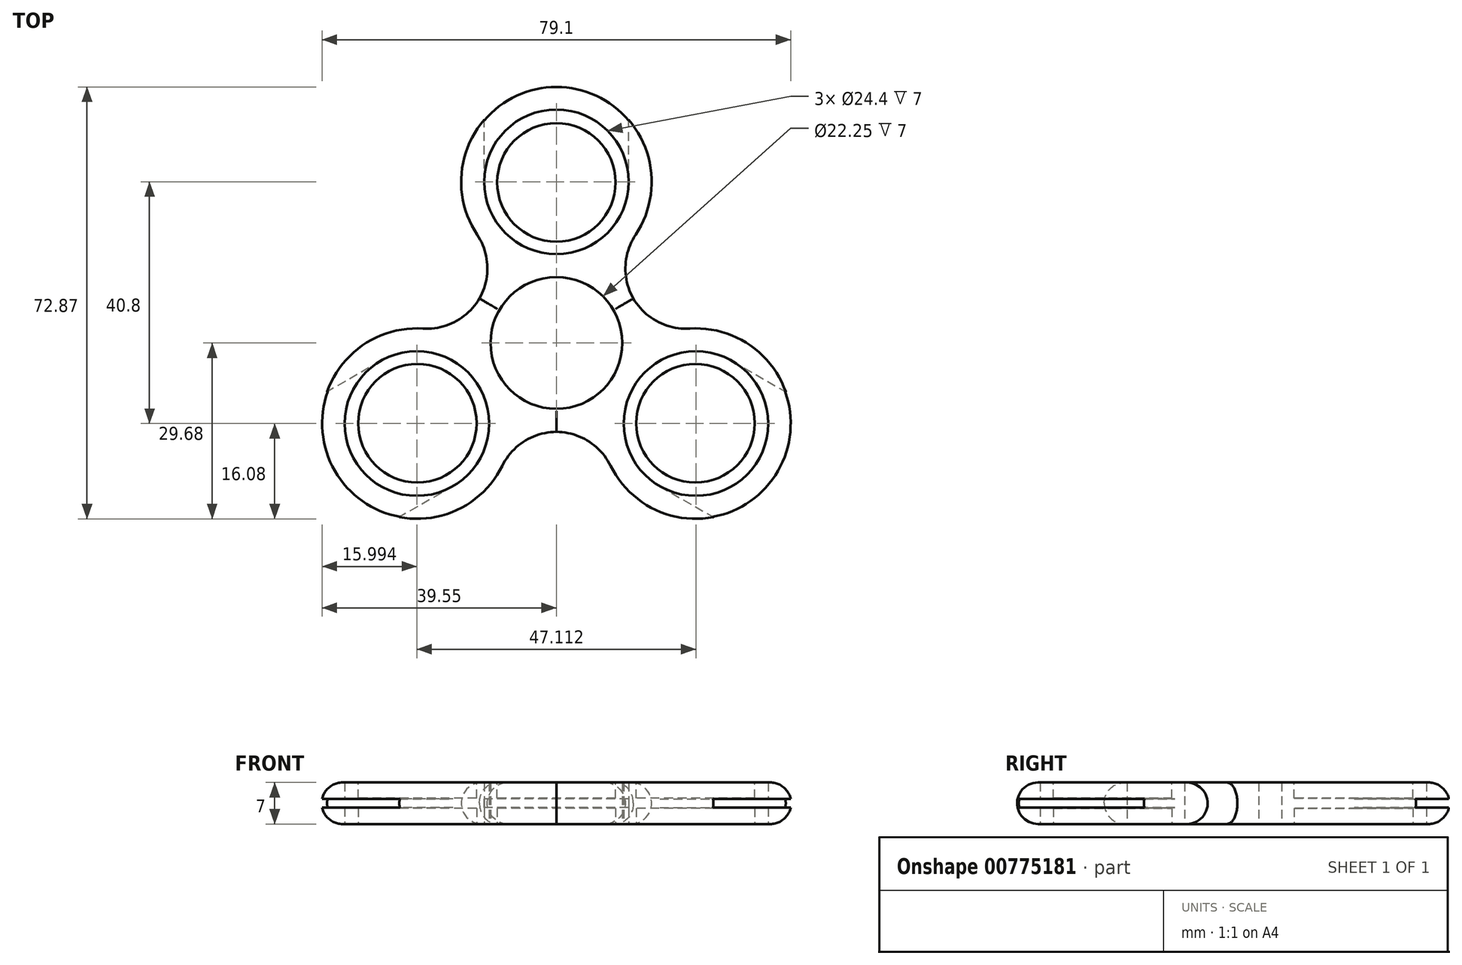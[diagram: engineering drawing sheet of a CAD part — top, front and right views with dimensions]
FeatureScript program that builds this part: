
annotation { "Feature Type Name" : "Feature", "Feature Type Description" : "" }
export const myFeature = defineFeature(function(context is Context, id is Id, definition is map)
    precondition{}
    {
        {
            var Q0;
            Q0=qCreatedBy(makeId("Top.planeOp"),FACE);
            var sketch = newSketch(context, id + "F0", { "sketchPlane" : qUnion([Q0])});
            skCircle(sketch, "E0", {"center": v(0, 0) * mm, "radius": 15 * mm});
            skCircle(sketch, "E1", {"center": v(0, 0) * mm, "radius": 11.12 * mm});
            skCircle(sketch, "E2", {"center": v(0, 27.2) * mm, "radius": 12.2 * mm});
            skCircle(sketch, "E3", {"center": v(0, 27.2) * mm, "radius": 16.07 * mm});
            skLineSegment(sketch, "E4", {"start": v(-12.2, 27.2) * mm, "end": v(-12.2, 47.2) * mm});
            skLineSegment(sketch, "E5.MirrorCS", {"start": v(12.2, 27.2) * mm, "end": v(12.2, 47.2) * mm});
            skLineSegment(sketch, "E6", {"start": v(-12.2, 47.2) * mm, "end": v(12.2, 47.2) * mm});
            skCircle(sketch, "E7.MirrorC", {"center": v(0, 27.1) * mm, "radius": 10 * mm});
            skCircle(sketch, "E8.1.0", {"center": v(-23.56, -13.6) * mm, "radius": 16.07 * mm});
            skCircle(sketch, "E8.1.1", {"center": v(-23.56, -13.6) * mm, "radius": 12.2 * mm});
            skCircle(sketch, "E8.1.2", {"center": v(-23.47, -13.55) * mm, "radius": 10 * mm});
            skLineSegment(sketch, "E8.1.3", {"start": v(-17.46, -24.17) * mm, "end": v(-34.78, -34.17) * mm});
            skLineSegment(sketch, "E8.1.4", {"start": v(-34.78, -34.17) * mm, "end": v(-46.98, -13.03) * mm});
            skLineSegment(sketch, "E8.1.5", {"start": v(-29.66, -3.03) * mm, "end": v(-46.98, -13.03) * mm});
            skCircle(sketch, "E8.2.0", {"center": v(23.56, -13.6) * mm, "radius": 16.07 * mm});
            skCircle(sketch, "E8.2.1", {"center": v(23.56, -13.6) * mm, "radius": 12.2 * mm});
            skCircle(sketch, "E8.2.2", {"center": v(23.47, -13.55) * mm, "radius": 10 * mm});
            skLineSegment(sketch, "E8.2.3", {"start": v(29.66, -3.03) * mm, "end": v(46.98, -13.03) * mm});
            skLineSegment(sketch, "E8.2.4", {"start": v(46.98, -13.03) * mm, "end": v(34.78, -34.17) * mm});
            skLineSegment(sketch, "E8.2.5", {"start": v(17.46, -24.17) * mm, "end": v(34.78, -34.17) * mm});
            skSolve(sketch);
        }
        {
            var Q0;
            {var subQ0=sQuery(id+"F0.wireOp",EDGE,"E3");var subQ1=sQuery(id+"F0.wireOp",EDGE,"E0");var subQ2=makeQuery(id+"F0.imprint","INTERSECT",VERTEX,{"disambiguationData":[OD(0.0)],"derivedFrom":[subQ1,subQ0]});Q0=makeQuery(id+"F0.imprint","IMPRINT",FACE,{"disambiguationData":[TD([[makeQuery(id+"F0.imprint","IMPRINT",EDGE,{"disambiguationData":[TD([[subQ2,-1.0]])],"derivedFrom":subQ1}),-1.0]])]});}
            var Q1;
            {var subQ0=sQuery(id+"F0.wireOp",EDGE,"E3");var subQ1=sQuery(id+"F0.wireOp",EDGE,"E0");var subQ2=makeQuery(id+"F0.imprint","INTERSECT",VERTEX,{"disambiguationData":[OD(1.0)],"derivedFrom":[subQ1,subQ0]});Q1=makeQuery(id+"F0.imprint","IMPRINT",FACE,{"disambiguationData":[TD([[makeQuery(id+"F0.imprint","IMPRINT",EDGE,{"disambiguationData":[TD([[subQ2,1.0]])],"derivedFrom":subQ1}),-1.0]])]});}
            var Q2;
            {var subQ0=sQuery(id+"F0.wireOp",EDGE,"E3");var subQ1=sQuery(id+"F0.wireOp",EDGE,"E0");var subQ2=makeQuery(id+"F0.imprint","INTERSECT",VERTEX,{"disambiguationData":[OD(1.0)],"derivedFrom":[subQ1,subQ0]});Q2=makeQuery(id+"F0.imprint","IMPRINT",FACE,{"disambiguationData":[TD([[makeQuery(id+"F0.imprint","IMPRINT",EDGE,{"disambiguationData":[TD([[subQ2,-1.0]])],"derivedFrom":subQ1}),1.0]])]});}
            var Q3;
            {var subQ0=sQuery(id+"F0.wireOp",EDGE,"E3");var subQ1=sQuery(id+"F0.wireOp",EDGE,"E0");var subQ2=makeQuery(id+"F0.imprint","INTERSECT",VERTEX,{"disambiguationData":[OD(0.0)],"derivedFrom":[subQ1,subQ0]});Q3=makeQuery(id+"F0.imprint","IMPRINT",FACE,{"disambiguationData":[TD([[makeQuery(id+"F0.imprint","IMPRINT",EDGE,{"disambiguationData":[TD([[subQ2,-1.0]])],"derivedFrom":subQ1}),1.0]])]});}
            var Q4;
            {var subQ0=sQuery(id+"F0.wireOp",EDGE,"E3");var subQ1=sQuery(id+"F0.wireOp",EDGE,"E0");var subQ2=makeQuery(id+"F0.imprint","INTERSECT",VERTEX,{"disambiguationData":[OD(0.0)],"derivedFrom":[subQ1,subQ0]});Q4=makeQuery(id+"F0.imprint","IMPRINT",FACE,{"disambiguationData":[TD([[makeQuery(id+"F0.imprint","IMPRINT",EDGE,{"disambiguationData":[TD([[subQ2,1.0]])],"derivedFrom":subQ1}),1.0]])]});}
            var Q5;
            {var subQ0=sQuery(id+"F0.wireOp",EDGE,"f69440ca-244b-4b86-9447-29ce6fa7a21b0.MirrorC");var subQ1=sQuery(id+"F0.wireOp",EDGE,"E0");var subQ2=makeQuery(id+"F0.imprint","INTERSECT",VERTEX,{"disambiguationData":[OD(0.0)],"derivedFrom":[subQ1,subQ0]});Q5=makeQuery(id+"F0.imprint","IMPRINT",FACE,{"disambiguationData":[TD([[makeQuery(id+"F0.imprint","IMPRINT",EDGE,{"disambiguationData":[TD([[subQ2,-1.0]])],"derivedFrom":subQ1}),1.0]])]});}
            var Q6;
            {var subQ0=sQuery(id+"F0.wireOp",EDGE,"f69440ca-244b-4b86-9447-29ce6fa7a21b0.MirrorC");var subQ1=sQuery(id+"F0.wireOp",EDGE,"E0");var subQ2=makeQuery(id+"F0.imprint","INTERSECT",VERTEX,{"disambiguationData":[OD(0.0)],"derivedFrom":[subQ1,subQ0]});Q6=makeQuery(id+"F0.imprint","IMPRINT",FACE,{"disambiguationData":[TD([[makeQuery(id+"F0.imprint","IMPRINT",EDGE,{"disambiguationData":[TD([[subQ2,-1.0]])],"derivedFrom":subQ1}),-1.0]])]});}
            var Q7;
            {var subQ0=sQuery(id+"F0.wireOp",EDGE,"f69440ca-244b-4b86-9447-29ce6fa7a21b0.MirrorC");var subQ1=sQuery(id+"F0.wireOp",EDGE,"E0");var subQ2=makeQuery(id+"F0.imprint","INTERSECT",VERTEX,{"disambiguationData":[OD(1.0)],"derivedFrom":[subQ1,subQ0]});Q7=makeQuery(id+"F0.imprint","IMPRINT",FACE,{"disambiguationData":[TD([[makeQuery(id+"F0.imprint","IMPRINT",EDGE,{"disambiguationData":[TD([[subQ2,1.0]])],"derivedFrom":subQ1}),-1.0]])]});}
            var Q8;
            {var subQ0=sQuery(id+"F0.wireOp",EDGE,"E8.1.0");var subQ1=sQuery(id+"F0.wireOp",EDGE,"E0");var subQ2=makeQuery(id+"F0.imprint","INTERSECT",VERTEX,{"disambiguationData":[OD(0.0)],"derivedFrom":[subQ1,subQ0]});Q8=makeQuery(id+"F0.imprint","IMPRINT",FACE,{"disambiguationData":[TD([[makeQuery(id+"F0.imprint","IMPRINT",EDGE,{"disambiguationData":[TD([[subQ2,-1.0]])],"derivedFrom":subQ1}),-1.0]])]});}
            var Q9;
            {var subQ0=sQuery(id+"F0.wireOp",EDGE,"E8.1.0");var subQ1=sQuery(id+"F0.wireOp",EDGE,"E0");var subQ2=makeQuery(id+"F0.imprint","INTERSECT",VERTEX,{"disambiguationData":[OD(0.0)],"derivedFrom":[subQ1,subQ0]});Q9=makeQuery(id+"F0.imprint","IMPRINT",FACE,{"disambiguationData":[TD([[makeQuery(id+"F0.imprint","IMPRINT",EDGE,{"disambiguationData":[TD([[subQ2,-1.0]])],"derivedFrom":subQ1}),1.0]])]});}
            var Q10;
            {var subQ0=sQuery(id+"F0.wireOp",EDGE,"E8.1.0");var subQ1=sQuery(id+"F0.wireOp",EDGE,"E0");var subQ2=makeQuery(id+"F0.imprint","INTERSECT",VERTEX,{"disambiguationData":[OD(1.0)],"derivedFrom":[subQ1,subQ0]});Q10=makeQuery(id+"F0.imprint","IMPRINT",FACE,{"disambiguationData":[TD([[makeQuery(id+"F0.imprint","IMPRINT",EDGE,{"disambiguationData":[TD([[subQ2,1.0]])],"derivedFrom":subQ1}),-1.0]])]});}
            var Q11;
            {var subQ0=sQuery(id+"F0.wireOp",EDGE,"E8.1.0");var subQ1=sQuery(id+"F0.wireOp",EDGE,"E0");var subQ2=makeQuery(id+"F0.imprint","INTERSECT",VERTEX,{"disambiguationData":[OD(1.0)],"derivedFrom":[subQ1,subQ0]});Q11=makeQuery(id+"F0.imprint","IMPRINT",FACE,{"disambiguationData":[TD([[makeQuery(id+"F0.imprint","IMPRINT",EDGE,{"disambiguationData":[TD([[subQ2,-1.0]])],"derivedFrom":subQ1}),1.0]])]});}
            var Q12;
            {var subQ0=sQuery(id+"F0.wireOp",EDGE,"E8.2.0");var subQ1=sQuery(id+"F0.wireOp",EDGE,"E0");var subQ2=makeQuery(id+"F0.imprint","INTERSECT",VERTEX,{"disambiguationData":[OD(1.0)],"derivedFrom":[subQ1,subQ0]});Q12=makeQuery(id+"F0.imprint","IMPRINT",FACE,{"disambiguationData":[TD([[makeQuery(id+"F0.imprint","IMPRINT",EDGE,{"disambiguationData":[TD([[subQ2,-1.0]])],"derivedFrom":subQ1}),1.0]])]});}
            var Q13;
            {var subQ0=sQuery(id+"F0.wireOp",EDGE,"E8.2.0");var subQ1=sQuery(id+"F0.wireOp",EDGE,"E0");var subQ2=makeQuery(id+"F0.imprint","INTERSECT",VERTEX,{"disambiguationData":[OD(1.0)],"derivedFrom":[subQ1,subQ0]});Q13=makeQuery(id+"F0.imprint","IMPRINT",FACE,{"disambiguationData":[TD([[makeQuery(id+"F0.imprint","IMPRINT",EDGE,{"disambiguationData":[TD([[subQ2,-1.0]])],"derivedFrom":subQ1}),-1.0]])]});}
            var Q14;
            {var subQ0=sQuery(id+"F0.wireOp",EDGE,"E8.2.0");var subQ1=sQuery(id+"F0.wireOp",EDGE,"E0");var subQ2=makeQuery(id+"F0.imprint","INTERSECT",VERTEX,{"disambiguationData":[OD(0.0)],"derivedFrom":[subQ1,subQ0]});Q14=makeQuery(id+"F0.imprint","IMPRINT",FACE,{"disambiguationData":[TD([[makeQuery(id+"F0.imprint","IMPRINT",EDGE,{"disambiguationData":[TD([[subQ2,1.0]])],"derivedFrom":subQ1}),-1.0]])]});}
            extrude(context, id + "F1", {"entities" : qUnion([Q0, Q1, Q2, Q3, Q4, Q5, Q6, Q7, Q8, Q9, Q10, Q11, Q12, Q13, Q14]), "depth" : 7 * mm, "offsetDistance" : 25 * mm});
        }
        {
            var Q0;
            {var subQ0=sQuery(id+"F0.wireOp",EDGE,"v1YN2P9r-Erew-ceTy-kHM2-pDfLZ22rBO5I");var subQ1=sQuery(id+"F0.wireOp",EDGE,"aa156850-8edd-4638-87e1-16b269d65bfe0.MirrorC");var subQ2=makeQuery(id+"F0.imprint","INTERSECT",VERTEX,{"derivedFrom":[subQ1,subQ0]});Q0=makeQuery(id+"F0.imprint","IMPRINT",FACE,{"disambiguationData":[TD([[makeQuery(id+"F0.imprint","IMPRINT",EDGE,{"disambiguationData":[TD([[subQ2,1.0]])],"derivedFrom":subQ1}),1.0]])]});}
            var Q1;
            {var subQ0=sQuery(id+"F0.wireOp",EDGE,"E4");var subQ1=sQuery(id+"F0.wireOp",EDGE,"E2");var subQ2=makeQuery(id+"F0.imprint","INTERSECT",VERTEX,{"derivedFrom":[subQ1,subQ0]});Q1=makeQuery(id+"F0.imprint","IMPRINT",FACE,{"disambiguationData":[TD([[makeQuery(id+"F0.imprint","IMPRINT",EDGE,{"disambiguationData":[TD([[subQ2,1.0]])],"derivedFrom":subQ1}),-1.0]])]});}
            var Q2;
            {var subQ3=sQuery(id+"F0.wireOp",EDGE,"E8.1.0");var subQ5=sQuery(id+"F0.wireOp",EDGE,"E8.1.4");var subQ6=makeQuery(id+"F0.imprint","INTERSECT",VERTEX,{"disambiguationData":[OD(0.0)],"derivedFrom":[subQ3,subQ5]});Q2=makeQuery(id+"F0.imprint","IMPRINT",FACE,{"disambiguationData":[TD([[makeQuery(id+"F0.imprint","IMPRINT",EDGE,{"disambiguationData":[TD([[subQ6,1.0]])],"derivedFrom":subQ3}),1.0]])]});}
            var Q3;
            {var subQ3=sQuery(id+"F0.wireOp",EDGE,"E8.2.0");var subQ5=sQuery(id+"F0.wireOp",EDGE,"E8.2.4");var subQ6=makeQuery(id+"F0.imprint","INTERSECT",VERTEX,{"disambiguationData":[OD(0.0)],"derivedFrom":[subQ3,subQ5]});Q3=makeQuery(id+"F0.imprint","IMPRINT",FACE,{"disambiguationData":[TD([[makeQuery(id+"F0.imprint","IMPRINT",EDGE,{"disambiguationData":[TD([[subQ6,1.0]])],"derivedFrom":subQ3}),1.0]])]});}
            var Q4;
            {var subQ0=sQuery(id+"F0.wireOp",EDGE,"E8.1.3");var subQ1=sQuery(id+"F0.wireOp",EDGE,"E8.1.0");var subQ2=makeQuery(id+"F0.imprint","INTERSECT",VERTEX,{"derivedFrom":[subQ1,subQ0]});Q4=makeQuery(id+"F0.imprint","IMPRINT",FACE,{"disambiguationData":[TD([[makeQuery(id+"F0.imprint","IMPRINT",EDGE,{"disambiguationData":[TD([[subQ2,1.0]])],"derivedFrom":subQ1}),1.0]])]});}
            var Q5;
            {var subQ0=sQuery(id+"F0.wireOp",EDGE,"E8.2.3");var subQ1=sQuery(id+"F0.wireOp",EDGE,"E8.2.0");var subQ2=makeQuery(id+"F0.imprint","INTERSECT",VERTEX,{"derivedFrom":[subQ1,subQ0]});Q5=makeQuery(id+"F0.imprint","IMPRINT",FACE,{"disambiguationData":[TD([[makeQuery(id+"F0.imprint","IMPRINT",EDGE,{"disambiguationData":[TD([[subQ2,1.0]])],"derivedFrom":subQ1}),1.0]])]});}
            extrude(context, id + "F2", {"entities" : qUnion([Q0, Q1, Q2, Q3, Q4, Q5]), "operationType" : NewBodyOperationType.ADD, "depth" : 2.75 * mm, "offsetDistance" : 25 * mm});
        }
        {
            var Q0;
            Q0=makeQuery(id+"F0.imprint","IMPRINT",FACE,{"disambiguationData":[TD([[makeQuery(id+"F0.imprint","IMPRINT",EDGE,{"derivedFrom":sQuery(id+"F0.wireOp",EDGE,"E7.MirrorC")}),1.0]])]});
            var Q1;
            Q1=makeQuery(id+"F0.imprint","IMPRINT",FACE,{"disambiguationData":[TD([[makeQuery(id+"F0.imprint","IMPRINT",EDGE,{"derivedFrom":sQuery(id+"F0.wireOp",EDGE,"AoGlkw56-T5SC-8iM1-7Erz-dF4ec4XMPC5s")}),-1.0]])]});
            var Q2;
            Q2=makeQuery(id+"F0.imprint","IMPRINT",FACE,{"disambiguationData":[TD([[makeQuery(id+"F0.imprint","IMPRINT",EDGE,{"derivedFrom":sQuery(id+"F0.wireOp",EDGE,"E8.1.2")}),1.0]])]});
            var Q3;
            Q3=makeQuery(id+"F0.imprint","IMPRINT",FACE,{"disambiguationData":[TD([[makeQuery(id+"F0.imprint","IMPRINT",EDGE,{"derivedFrom":sQuery(id+"F0.wireOp",EDGE,"E8.2.2")}),1.0]])]});
            extrude(context, id + "F3", {"entities" : qUnion([Q0, Q1, Q2, Q3]), "operationType" : NewBodyOperationType.ADD, "depth" : 2.67 * mm, "offsetDistance" : 25 * mm});
        }
        {
            var Q0;
            Q0=makeQuery(id+"F1.opExtrude","CAP_FACE",FACE,{"disambiguationData":[OSD([sQuery(id+"F0.wireOp",EDGE,"E0"),sQuery(id+"F0.wireOp",EDGE,"E1"),sQuery(id+"F0.wireOp",EDGE,"E2"),sQuery(id+"F0.wireOp",EDGE,"E3"),sQuery(id+"F0.wireOp",EDGE,"E4"),sQuery(id+"F0.wireOp",EDGE,"E5.MirrorCS"),sQuery(id+"F0.wireOp",EDGE,"E8.1.0"),sQuery(id+"F0.wireOp",EDGE,"E8.1.1"),sQuery(id+"F0.wireOp",EDGE,"E8.1.3"),sQuery(id+"F0.wireOp",EDGE,"E8.1.5"),sQuery(id+"F0.wireOp",EDGE,"E8.2.0"),sQuery(id+"F0.wireOp",EDGE,"E8.2.1"),sQuery(id+"F0.wireOp",EDGE,"E8.2.3"),sQuery(id+"F0.wireOp",EDGE,"E8.2.5")])],"isStart":false});
            var sketch = newSketch(context, id + "F4", { "sketchPlane" : qUnion([Q0])});
            skCircle(sketch, "E9", {"center": v(0, 0) * mm, "radius": 15 * mm});
            skCircle(sketch, "E10", {"center": v(0, 0) * mm, "radius": 11.12 * mm});
            skCircle(sketch, "E11", {"center": v(0, 27.2) * mm, "radius": 12.2 * mm});
            skCircle(sketch, "E12", {"center": v(0, 27.2) * mm, "radius": 16.07 * mm});
            skLineSegment(sketch, "E13", {"start": v(-12.2, 27.2) * mm, "end": v(-12.2, 47.2) * mm});
            skLineSegment(sketch, "E14.MirrorCS", {"start": v(12.2, 27.2) * mm, "end": v(12.2, 47.2) * mm});
            skLineSegment(sketch, "E15", {"start": v(-12.2, 47.2) * mm, "end": v(12.2, 47.2) * mm});
            skCircle(sketch, "E16.MirrorC", {"center": v(0, 27.1) * mm, "radius": 10 * mm});
            skCircle(sketch, "E17.1.0", {"center": v(-23.56, -13.6) * mm, "radius": 16.07 * mm});
            skCircle(sketch, "E17.1.1", {"center": v(-23.56, -13.6) * mm, "radius": 12.2 * mm});
            skCircle(sketch, "E17.1.2", {"center": v(-23.47, -13.55) * mm, "radius": 10 * mm});
            skLineSegment(sketch, "E17.1.3", {"start": v(-17.46, -24.17) * mm, "end": v(-34.78, -34.17) * mm});
            skLineSegment(sketch, "E17.1.4", {"start": v(-34.78, -34.17) * mm, "end": v(-46.98, -13.03) * mm});
            skLineSegment(sketch, "E17.1.5", {"start": v(-29.66, -3.03) * mm, "end": v(-46.98, -13.03) * mm});
            skCircle(sketch, "E17.2.0", {"center": v(23.56, -13.6) * mm, "radius": 16.07 * mm});
            skCircle(sketch, "E17.2.1", {"center": v(23.56, -13.6) * mm, "radius": 12.2 * mm});
            skCircle(sketch, "E17.2.2", {"center": v(23.47, -13.55) * mm, "radius": 10 * mm});
            skLineSegment(sketch, "E17.2.3", {"start": v(29.66, -3.03) * mm, "end": v(46.98, -13.03) * mm});
            skLineSegment(sketch, "E17.2.4", {"start": v(46.98, -13.03) * mm, "end": v(34.78, -34.17) * mm});
            skLineSegment(sketch, "E17.2.5", {"start": v(17.46, -24.17) * mm, "end": v(34.78, -34.17) * mm});
            skSolve(sketch);
        }
        {
            var Q0;
            {var subQ0=sQuery(id+"F4.wireOp",EDGE,"E13");var subQ1=sQuery(id+"F4.wireOp",EDGE,"E11");var subQ2=makeQuery(id+"F4.imprint","INTERSECT",VERTEX,{"derivedFrom":[subQ1,subQ0]});Q0=makeQuery(id+"F4.imprint","IMPRINT",FACE,{"disambiguationData":[TD([[makeQuery(id+"F4.imprint","IMPRINT",EDGE,{"disambiguationData":[TD([[subQ2,1.0]])],"derivedFrom":subQ1}),-1.0]])]});}
            var Q1;
            {var subQ0=sQuery(id+"F4.wireOp",EDGE,"E17.2.3");var subQ1=sQuery(id+"F4.wireOp",EDGE,"E17.2.0");var subQ2=makeQuery(id+"F4.imprint","INTERSECT",VERTEX,{"derivedFrom":[subQ1,subQ0]});Q1=makeQuery(id+"F4.imprint","IMPRINT",FACE,{"disambiguationData":[TD([[makeQuery(id+"F4.imprint","IMPRINT",EDGE,{"disambiguationData":[TD([[subQ2,1.0]])],"derivedFrom":subQ1}),1.0]])]});}
            var Q2;
            {var subQ0=sQuery(id+"F4.wireOp",EDGE,"E17.1.3");var subQ1=sQuery(id+"F4.wireOp",EDGE,"E17.1.0");var subQ2=makeQuery(id+"F4.imprint","INTERSECT",VERTEX,{"derivedFrom":[subQ1,subQ0]});Q2=makeQuery(id+"F4.imprint","IMPRINT",FACE,{"disambiguationData":[TD([[makeQuery(id+"F4.imprint","IMPRINT",EDGE,{"disambiguationData":[TD([[subQ2,1.0]])],"derivedFrom":subQ1}),1.0]])]});}
            extrude(context, id + "F5", {"entities" : qUnion([Q0, Q1, Q2]), "operationType" : NewBodyOperationType.ADD, "oppositeDirection" : true, "depth" : 2.75 * mm, "offsetDistance" : 25 * mm});
        }
        {
            var Q0;
            Q0=makeQuery(id+"F4.imprint","IMPRINT",FACE,{"disambiguationData":[TD([[makeQuery(id+"F4.imprint","IMPRINT",EDGE,{"derivedFrom":sQuery(id+"F4.wireOp",EDGE,"E17.1.2")}),1.0]])]});
            var Q1;
            Q1=makeQuery(id+"F4.imprint","IMPRINT",FACE,{"disambiguationData":[TD([[makeQuery(id+"F4.imprint","IMPRINT",EDGE,{"derivedFrom":sQuery(id+"F4.wireOp",EDGE,"E17.2.2")}),1.0]])]});
            var Q2;
            Q2=makeQuery(id+"F4.imprint","IMPRINT",FACE,{"disambiguationData":[TD([[makeQuery(id+"F4.imprint","IMPRINT",EDGE,{"derivedFrom":sQuery(id+"F4.wireOp",EDGE,"E16.MirrorC")}),1.0]])]});
            extrude(context, id + "F6", {"entities" : qUnion([Q0, Q1, Q2]), "operationType" : NewBodyOperationType.ADD, "oppositeDirection" : true, "depth" : 2.67 * mm, "offsetDistance" : 25 * mm});
        }
        {
            var Q0;
            {var subQ0=sQuery(id+"F0.wireOp",EDGE,"E8.1.0");var subQ1=sQuery(id+"F0.wireOp",EDGE,"E0");Q0=makeQuery(id+"F1.opExtrude","SWEPT_EDGE",EDGE,{"disambiguationData":[OSD([subQ1,subQ0]),TDD([makeQuery(id+"F0.imprint","INTERSECT",VERTEX,{"disambiguationData":[OD(1.0)],"derivedFrom":[subQ1,subQ0]})])]});}
            var Q1;
            {var subQ0=sQuery(id+"F0.wireOp",EDGE,"E8.2.0");var subQ1=sQuery(id+"F0.wireOp",EDGE,"E0");Q1=makeQuery(id+"F1.opExtrude","SWEPT_EDGE",EDGE,{"disambiguationData":[OSD([subQ1,subQ0]),TDD([makeQuery(id+"F0.imprint","INTERSECT",VERTEX,{"disambiguationData":[OD(1.0)],"derivedFrom":[subQ1,subQ0]})])]});}
            var Q2;
            {var subQ0=sQuery(id+"F0.wireOp",EDGE,"E8.2.0");var subQ1=sQuery(id+"F0.wireOp",EDGE,"E0");Q2=makeQuery(id+"F1.opExtrude","SWEPT_EDGE",EDGE,{"disambiguationData":[OSD([subQ1,subQ0]),TDD([makeQuery(id+"F0.imprint","INTERSECT",VERTEX,{"disambiguationData":[OD(0.0)],"derivedFrom":[subQ1,subQ0]})])]});}
            var Q3;
            {var subQ0=sQuery(id+"F0.wireOp",EDGE,"E3");var subQ1=sQuery(id+"F0.wireOp",EDGE,"E0");Q3=makeQuery(id+"F1.opExtrude","SWEPT_EDGE",EDGE,{"disambiguationData":[OSD([subQ1,subQ0]),TDD([makeQuery(id+"F0.imprint","INTERSECT",VERTEX,{"disambiguationData":[OD(0.0)],"derivedFrom":[subQ1,subQ0]})])]});}
            var Q4;
            {var subQ0=sQuery(id+"F0.wireOp",EDGE,"E3");var subQ1=sQuery(id+"F0.wireOp",EDGE,"E0");Q4=makeQuery(id+"F1.opExtrude","SWEPT_EDGE",EDGE,{"disambiguationData":[OSD([subQ1,subQ0]),TDD([makeQuery(id+"F0.imprint","INTERSECT",VERTEX,{"disambiguationData":[OD(1.0)],"derivedFrom":[subQ1,subQ0]})])]});}
            var Q5;
            {var subQ0=sQuery(id+"F0.wireOp",EDGE,"E8.1.0");var subQ1=sQuery(id+"F0.wireOp",EDGE,"E0");Q5=makeQuery(id+"F1.opExtrude","SWEPT_EDGE",EDGE,{"disambiguationData":[OSD([subQ1,subQ0]),TDD([makeQuery(id+"F0.imprint","INTERSECT",VERTEX,{"disambiguationData":[OD(0.0)],"derivedFrom":[subQ1,subQ0]})])]});}
            fillet(context, id + "F7", {"entities" : qUnion([Q0, Q1, Q2, Q3, Q4, Q5]), "radius" : 10.3 * mm, "tangentPropagation" : true, "allowEdgeOverflow" : false});
        }
        {
            var Q0;
            {var subQ0=sQuery(id+"F4.wireOp",EDGE,"E17.2.1");var subQ1=sQuery(id+"F4.wireOp",EDGE,"E17.1.1");var subQ2=sQuery(id+"F4.wireOp",EDGE,"E11");var subQ3=sQuery(id+"F0.wireOp",EDGE,"E3");var subQ4=sQuery(id+"F0.wireOp",EDGE,"E0");Q0=makeQuery(id+"F7.opFillet","BLEND_EDGE",EDGE,{"blendedFrom":[makeQuery(id+"F1.opExtrude","SWEPT_EDGE",EDGE,{"disambiguationData":[OSD([subQ4,subQ3]),TDD([makeQuery(id+"F0.imprint","INTERSECT",VERTEX,{"disambiguationData":[OD(0.0)],"derivedFrom":[subQ4,subQ3]})])]}),makeQuery(id+"F6.boolean.opBoolean","MERGE",FACE,{"derivedFrom":[makeQuery(id+"F5.boolean.opBoolean","MERGE",FACE,{"derivedFrom":[makeQuery(id+"F1.opExtrude","CAP_FACE",FACE,{"disambiguationData":[OSD([subQ4,sQuery(id+"F0.wireOp",EDGE,"E1"),sQuery(id+"F0.wireOp",EDGE,"E2"),subQ3,sQuery(id+"F0.wireOp",EDGE,"E4"),sQuery(id+"F0.wireOp",EDGE,"E5.MirrorCS"),sQuery(id+"F0.wireOp",EDGE,"E8.1.0"),sQuery(id+"F0.wireOp",EDGE,"E8.1.1"),sQuery(id+"F0.wireOp",EDGE,"E8.1.3"),sQuery(id+"F0.wireOp",EDGE,"E8.1.5"),sQuery(id+"F0.wireOp",EDGE,"E8.2.0"),sQuery(id+"F0.wireOp",EDGE,"E8.2.1"),sQuery(id+"F0.wireOp",EDGE,"E8.2.3"),sQuery(id+"F0.wireOp",EDGE,"E8.2.5")])],"isStart":false}),makeQuery(id+"F5.opExtrude","CAP_FACE",FACE,{"disambiguationData":[OSD([subQ2,sQuery(id+"F4.wireOp",EDGE,"E12"),sQuery(id+"F4.wireOp",EDGE,"E13"),sQuery(id+"F4.wireOp",EDGE,"E14.MirrorCS")])],"isStart":true}),makeQuery(id+"F5.opExtrude","CAP_FACE",FACE,{"disambiguationData":[OSD([sQuery(id+"F4.wireOp",EDGE,"E17.1.0"),subQ1,sQuery(id+"F4.wireOp",EDGE,"E17.1.3"),sQuery(id+"F4.wireOp",EDGE,"E17.1.5")])],"isStart":true}),makeQuery(id+"F5.opExtrude","CAP_FACE",FACE,{"disambiguationData":[OSD([sQuery(id+"F4.wireOp",EDGE,"E17.2.0"),subQ0,sQuery(id+"F4.wireOp",EDGE,"E17.2.3"),sQuery(id+"F4.wireOp",EDGE,"E17.2.5")])],"isStart":true})]}),makeQuery(id+"F6.opExtrude","CAP_FACE",FACE,{"disambiguationData":[OSD([subQ2,sQuery(id+"F4.wireOp",EDGE,"E16.MirrorC")])],"isStart":true}),makeQuery(id+"F6.opExtrude","CAP_FACE",FACE,{"disambiguationData":[OSD([subQ1,sQuery(id+"F4.wireOp",EDGE,"E17.1.2")])],"isStart":true}),makeQuery(id+"F6.opExtrude","CAP_FACE",FACE,{"disambiguationData":[OSD([subQ0,sQuery(id+"F4.wireOp",EDGE,"E17.2.2")])],"isStart":true})]})],"blendedInto":[makeQuery(id+"F6.boolean.opBoolean","MERGE",FACE,{"derivedFrom":[makeQuery(id+"F5.boolean.opBoolean","MERGE",FACE,{"derivedFrom":[makeQuery(id+"F1.opExtrude","CAP_FACE",FACE,{"disambiguationData":[OSD([subQ4,sQuery(id+"F0.wireOp",EDGE,"E1"),sQuery(id+"F0.wireOp",EDGE,"E2"),subQ3,sQuery(id+"F0.wireOp",EDGE,"E4"),sQuery(id+"F0.wireOp",EDGE,"E5.MirrorCS"),sQuery(id+"F0.wireOp",EDGE,"E8.1.0"),sQuery(id+"F0.wireOp",EDGE,"E8.1.1"),sQuery(id+"F0.wireOp",EDGE,"E8.1.3"),sQuery(id+"F0.wireOp",EDGE,"E8.1.5"),sQuery(id+"F0.wireOp",EDGE,"E8.2.0"),sQuery(id+"F0.wireOp",EDGE,"E8.2.1"),sQuery(id+"F0.wireOp",EDGE,"E8.2.3"),sQuery(id+"F0.wireOp",EDGE,"E8.2.5")])],"isStart":false}),makeQuery(id+"F5.opExtrude","CAP_FACE",FACE,{"disambiguationData":[OSD([subQ2,sQuery(id+"F4.wireOp",EDGE,"E12"),sQuery(id+"F4.wireOp",EDGE,"E13"),sQuery(id+"F4.wireOp",EDGE,"E14.MirrorCS")])],"isStart":true}),makeQuery(id+"F5.opExtrude","CAP_FACE",FACE,{"disambiguationData":[OSD([sQuery(id+"F4.wireOp",EDGE,"E17.1.0"),subQ1,sQuery(id+"F4.wireOp",EDGE,"E17.1.3"),sQuery(id+"F4.wireOp",EDGE,"E17.1.5")])],"isStart":true}),makeQuery(id+"F5.opExtrude","CAP_FACE",FACE,{"disambiguationData":[OSD([sQuery(id+"F4.wireOp",EDGE,"E17.2.0"),subQ0,sQuery(id+"F4.wireOp",EDGE,"E17.2.3"),sQuery(id+"F4.wireOp",EDGE,"E17.2.5")])],"isStart":true})]}),makeQuery(id+"F6.opExtrude","CAP_FACE",FACE,{"disambiguationData":[OSD([subQ2,sQuery(id+"F4.wireOp",EDGE,"E16.MirrorC")])],"isStart":true}),makeQuery(id+"F6.opExtrude","CAP_FACE",FACE,{"disambiguationData":[OSD([subQ1,sQuery(id+"F4.wireOp",EDGE,"E17.1.2")])],"isStart":true}),makeQuery(id+"F6.opExtrude","CAP_FACE",FACE,{"disambiguationData":[OSD([subQ0,sQuery(id+"F4.wireOp",EDGE,"E17.2.2")])],"isStart":true})]})]});}
            var Q1;
            {var subQ0=sQuery(id+"F0.wireOp",EDGE,"E8.1.0");var subQ1=sQuery(id+"F0.wireOp",EDGE,"E0");Q1=makeQuery(id+"F5.boolean.opBoolean","MERGE",EDGE,{"derivedFrom":[makeQuery(id+"F1.opExtrude","CAP_EDGE",EDGE,{"disambiguationData":[OSD([subQ0]),TDD([makeQuery(id+"F0.imprint","IMPRINT",EDGE,{"disambiguationData":[TD([[makeQuery(id+"F0.imprint","INTERSECT",VERTEX,{"disambiguationData":[OD(1.0)],"derivedFrom":[subQ1,subQ0]}),1.0]])],"derivedFrom":subQ0})])],"isStart":false}),makeQuery(id+"F1.opExtrude","CAP_EDGE",EDGE,{"disambiguationData":[OSD([subQ0]),TDD([makeQuery(id+"F0.imprint","IMPRINT",EDGE,{"disambiguationData":[TD([[makeQuery(id+"F0.imprint","INTERSECT",VERTEX,{"disambiguationData":[OD(0.0)],"derivedFrom":[subQ1,subQ0]}),-1.0]])],"derivedFrom":subQ0})])],"isStart":false}),makeQuery(id+"F5.opExtrude","CAP_EDGE",EDGE,{"disambiguationData":[OSD([sQuery(id+"F4.wireOp",EDGE,"E17.1.0")])],"isStart":true})]});}
            var Q2;
            {var subQ0=sQuery(id+"F0.wireOp",EDGE,"E8.2.0");var subQ1=sQuery(id+"F0.wireOp",EDGE,"E0");Q2=makeQuery(id+"F5.boolean.opBoolean","MERGE",EDGE,{"derivedFrom":[makeQuery(id+"F1.opExtrude","CAP_EDGE",EDGE,{"disambiguationData":[OSD([subQ0]),TDD([makeQuery(id+"F0.imprint","IMPRINT",EDGE,{"disambiguationData":[TD([[makeQuery(id+"F0.imprint","INTERSECT",VERTEX,{"disambiguationData":[OD(0.0)],"derivedFrom":[subQ1,subQ0]}),1.0]])],"derivedFrom":subQ0})])],"isStart":false}),makeQuery(id+"F1.opExtrude","CAP_EDGE",EDGE,{"disambiguationData":[OSD([subQ0]),TDD([makeQuery(id+"F0.imprint","IMPRINT",EDGE,{"disambiguationData":[TD([[makeQuery(id+"F0.imprint","INTERSECT",VERTEX,{"disambiguationData":[OD(1.0)],"derivedFrom":[subQ1,subQ0]}),-1.0]])],"derivedFrom":subQ0})])],"isStart":false}),makeQuery(id+"F5.opExtrude","CAP_EDGE",EDGE,{"disambiguationData":[OSD([sQuery(id+"F4.wireOp",EDGE,"E17.2.0")])],"isStart":true})]});}
            var Q3;
            {var subQ0=sQuery(id+"F0.wireOp",EDGE,"E8.2.1");var subQ1=sQuery(id+"F0.wireOp",EDGE,"E8.1.1");var subQ2=sQuery(id+"F0.wireOp",EDGE,"E2");var subQ3=sQuery(id+"F0.wireOp",EDGE,"E8.1.5");var subQ4=sQuery(id+"F0.wireOp",EDGE,"E8.1.3");var subQ5=sQuery(id+"F0.wireOp",EDGE,"E8.1.0");var subQ6=sQuery(id+"F0.wireOp",EDGE,"E5.MirrorCS");var subQ7=sQuery(id+"F0.wireOp",EDGE,"E4");var subQ8=sQuery(id+"F0.wireOp",EDGE,"E3");var subQ9=sQuery(id+"F0.wireOp",EDGE,"E8.2.5");var subQ10=sQuery(id+"F0.wireOp",EDGE,"E8.2.0");var subQ11=sQuery(id+"F0.wireOp",EDGE,"E0");Q3=makeQuery(id+"F7.opFillet","BLEND_EDGE",EDGE,{"blendedFrom":[makeQuery(id+"F1.opExtrude","SWEPT_EDGE",EDGE,{"disambiguationData":[OSD([subQ11,subQ5]),TDD([makeQuery(id+"F0.imprint","INTERSECT",VERTEX,{"disambiguationData":[OD(1.0)],"derivedFrom":[subQ11,subQ5]})])]}),makeQuery(id+"F3.boolean.opBoolean","MERGE",FACE,{"derivedFrom":[makeQuery(id+"F2.boolean.opBoolean","MERGE",FACE,{"derivedFrom":[makeQuery(id+"F1.opExtrude","CAP_FACE",FACE,{"disambiguationData":[OSD([subQ11,sQuery(id+"F0.wireOp",EDGE,"E1"),subQ2,subQ8,subQ7,subQ6,subQ5,subQ1,subQ4,subQ3,subQ10,subQ0,sQuery(id+"F0.wireOp",EDGE,"E8.2.3"),subQ9])],"isStart":true}),makeQuery(id+"F2.opExtrude","CAP_FACE",FACE,{"disambiguationData":[OSD([subQ11,subQ10,subQ0,subQ9])],"isStart":true}),makeQuery(id+"F2.opExtrude","CAP_FACE",FACE,{"disambiguationData":[OSD([subQ2,subQ8,subQ7,subQ6])],"isStart":true}),makeQuery(id+"F2.opExtrude","CAP_FACE",FACE,{"disambiguationData":[OSD([subQ5,subQ1,subQ4,subQ3])],"isStart":true})]}),makeQuery(id+"F3.opExtrude","CAP_FACE",FACE,{"disambiguationData":[OSD([subQ2,sQuery(id+"F0.wireOp",EDGE,"E7.MirrorC")])],"isStart":true}),makeQuery(id+"F3.opExtrude","CAP_FACE",FACE,{"disambiguationData":[OSD([subQ1,sQuery(id+"F0.wireOp",EDGE,"E8.1.2")])],"isStart":true}),makeQuery(id+"F3.opExtrude","CAP_FACE",FACE,{"disambiguationData":[OSD([subQ0,sQuery(id+"F0.wireOp",EDGE,"E8.2.2")])],"isStart":true})]})],"blendedInto":[makeQuery(id+"F3.boolean.opBoolean","MERGE",FACE,{"derivedFrom":[makeQuery(id+"F2.boolean.opBoolean","MERGE",FACE,{"derivedFrom":[makeQuery(id+"F1.opExtrude","CAP_FACE",FACE,{"disambiguationData":[OSD([subQ11,sQuery(id+"F0.wireOp",EDGE,"E1"),subQ2,subQ8,subQ7,subQ6,subQ5,subQ1,subQ4,subQ3,subQ10,subQ0,sQuery(id+"F0.wireOp",EDGE,"E8.2.3"),subQ9])],"isStart":true}),makeQuery(id+"F2.opExtrude","CAP_FACE",FACE,{"disambiguationData":[OSD([subQ11,subQ10,subQ0,subQ9])],"isStart":true}),makeQuery(id+"F2.opExtrude","CAP_FACE",FACE,{"disambiguationData":[OSD([subQ2,subQ8,subQ7,subQ6])],"isStart":true}),makeQuery(id+"F2.opExtrude","CAP_FACE",FACE,{"disambiguationData":[OSD([subQ5,subQ1,subQ4,subQ3])],"isStart":true})]}),makeQuery(id+"F3.opExtrude","CAP_FACE",FACE,{"disambiguationData":[OSD([subQ2,sQuery(id+"F0.wireOp",EDGE,"E7.MirrorC")])],"isStart":true}),makeQuery(id+"F3.opExtrude","CAP_FACE",FACE,{"disambiguationData":[OSD([subQ1,sQuery(id+"F0.wireOp",EDGE,"E8.1.2")])],"isStart":true}),makeQuery(id+"F3.opExtrude","CAP_FACE",FACE,{"disambiguationData":[OSD([subQ0,sQuery(id+"F0.wireOp",EDGE,"E8.2.2")])],"isStart":true})]})]});}
            var Q4;
            {var subQ0=sQuery(id+"F0.wireOp",EDGE,"E8.2.0");var subQ1=sQuery(id+"F0.wireOp",EDGE,"E0");Q4=makeQuery(id+"F2.boolean.opBoolean","MERGE",EDGE,{"derivedFrom":[makeQuery(id+"F1.opExtrude","CAP_EDGE",EDGE,{"disambiguationData":[OSD([subQ0]),TDD([makeQuery(id+"F0.imprint","IMPRINT",EDGE,{"disambiguationData":[TD([[makeQuery(id+"F0.imprint","INTERSECT",VERTEX,{"disambiguationData":[OD(0.0)],"derivedFrom":[subQ1,subQ0]}),1.0]])],"derivedFrom":subQ0})])],"isStart":true}),makeQuery(id+"F1.opExtrude","CAP_EDGE",EDGE,{"disambiguationData":[OSD([subQ0]),TDD([makeQuery(id+"F0.imprint","IMPRINT",EDGE,{"disambiguationData":[TD([[makeQuery(id+"F0.imprint","INTERSECT",VERTEX,{"disambiguationData":[OD(1.0)],"derivedFrom":[subQ1,subQ0]}),-1.0]])],"derivedFrom":subQ0})])],"isStart":true}),makeQuery(id+"F2.opExtrude","CAP_EDGE",EDGE,{"disambiguationData":[OSD([subQ0])],"isStart":true})]});}
            var Q5;
            {var subQ0=sQuery(id+"F0.wireOp",EDGE,"E3");var subQ1=sQuery(id+"F0.wireOp",EDGE,"E0");Q5=makeQuery(id+"F2.boolean.opBoolean","MERGE",EDGE,{"derivedFrom":[makeQuery(id+"F1.opExtrude","CAP_EDGE",EDGE,{"disambiguationData":[OSD([subQ0]),TDD([makeQuery(id+"F0.imprint","IMPRINT",EDGE,{"disambiguationData":[TD([[makeQuery(id+"F0.imprint","INTERSECT",VERTEX,{"disambiguationData":[OD(1.0)],"derivedFrom":[subQ1,subQ0]}),1.0]])],"derivedFrom":subQ0})])],"isStart":true}),makeQuery(id+"F1.opExtrude","CAP_EDGE",EDGE,{"disambiguationData":[OSD([subQ0]),TDD([makeQuery(id+"F0.imprint","IMPRINT",EDGE,{"disambiguationData":[TD([[makeQuery(id+"F0.imprint","INTERSECT",VERTEX,{"disambiguationData":[OD(0.0)],"derivedFrom":[subQ1,subQ0]}),-1.0]])],"derivedFrom":subQ0})])],"isStart":true}),makeQuery(id+"F2.opExtrude","CAP_EDGE",EDGE,{"disambiguationData":[OSD([subQ0])],"isStart":true})]});}
            fillet(context, id + "F8", {"entities" : qUnion([Q0, Q1, Q2, Q3, Q4, Q5]), "radius" : 3.5 * mm, "tangentPropagation" : true, "allowEdgeOverflow" : false});
        }
    });
